AUTODESK INVENTOR PART (.ipt)
format: ipt  version: 2021 (Build 250183000, 183)  size: 1,086,976 bytes
history: native  units: mm
features: other x23, sketch x6, extrude x4, loft x3, pattern_circular x3
ambient origin geometry x6: Origin, XZ Plane, X Axis, Y Axis, Z Axis, Center Point
bodies: Solid1 (feature_tree)
feature tree (39):
  other  "Oberster Punkt"
  other  "Netzebene2"
  other  "Zahnradkörper"
  other  "Startpunkt"
  other  "Zahnebene"
  other  "Startskizze"
  other  "Endpunkt"
  loft  "Loft"
  pattern_circular  "Circular Pattern"  [2 undecoded]
  other  "3D-Skizze rechts"
  other  "Endebene rechts"
  loft  "Erhebung rechts"
  pattern_circular  "Runde Anordnung rechts"  [2 undecoded]
  other  "3D-Skizze links"
  other  "Endebene links"
  loft  "Erhebung links"
  pattern_circular  "Runde Anordnung links"  [2 undecoded]
  other  "Festkörper"
  extrude  "Extrusion1"  Depth=1.0mm
  extrude  "Extrusion2"  TaperAngle=0.0deg  [1 undecoded]
  extrude  "Extrusion3"  Depth=1.0mm TaperAngle=0.0deg
  extrude  "Extrusion4"  TaperAngle=360.0deg  [1 undecoded]
  other  "Netzebene"
  other  "Oberste Ebene"
  sketch  "Skizze des Zahnradkörpers"  dims[d7=7.765897mm d8=8.312228mm d9=18.082831mm d11=8.565mm d12=4.630354mm d15=4.9561mm d16=10.781744mm d17=0.0mm d18=90.0deg d19=0.0mm d20=90.0deg d21=200.0mm d22=360.0deg d26=146.848698mm d27=6.05637mm d28=30.0mm d29=-7.853982mm d30=4.630354mm d31=4.9561mm d32=10.781744mm d35=0.0mm d37=0.0mm d39=0.0mm d40=90.0deg d41=200.0mm d42=360.0deg d46=90.0deg d47=90.0deg d48=0.0mm d49=0.0mm d50=90.0deg d51=1.570796mm d52=0.0mm d53=0.0mm d54=0.0mm d56=6.859758mm d57=23.703203mm d58=19.017203mm d59=14.132846mm d60=11.338856mm d61=14.132846mm d62=11.338856mm d65=146.848698mm d66=31.5mm d67=30.0mm d68=-7.853982mm d69=6.05637mm d70=4.9561mm d71=10.781744mm d72=4.630354mm d73=11.338856mm d74=14.132846mm d75=0.0mm d77=0.0mm d79=0.0mm d80=90.0deg d81=200.0mm d82=360.0deg d84=10.0mm d85=20.0mm d86=20.0mm d87=10.0mm d88=0.0mm d89=0.0mm d90=90.0deg d91=90.0deg d92=90.0deg d93=90.0deg d96=3.5mm d97=0.0mm d98=10.0mm d99=10.0mm d100=7.0mm d101=1.0mm d102=0.0mm d103=3.2mm d104=1.0mm d105=0.0mm d106=15.5mm d107=18.0mm d108=3.0mm d109=0.0mm]
  other  "Endebene"
  other  "Endskizze"
  other  "Helical Curve Left"
  other  "Endskizze links"
  other  "Körperskizze"
  sketch  "Sketch6"  dims[d0=30.0mm d1=27.454416mm]
  other  "Srf1"
  other  "Helical Curve Right"
  other  "Endskizze rechts"
  sketch  "Skizze8"  dims[d2=32.12132mm]
  sketch  "Skizze9"  dims[d3=8.4mm]
  sketch  "Skizze10"  dims[d4=13.93934mm]
  sketch  "Skizze11"  dims[d5=90.0deg]
  other  "Flankendurchmesser"
note: 8 required parameter values undecoded (feature->parameter linkage not recoverable at this tier; creation-order binding heuristic only, values carry confidence <= 0.55)
